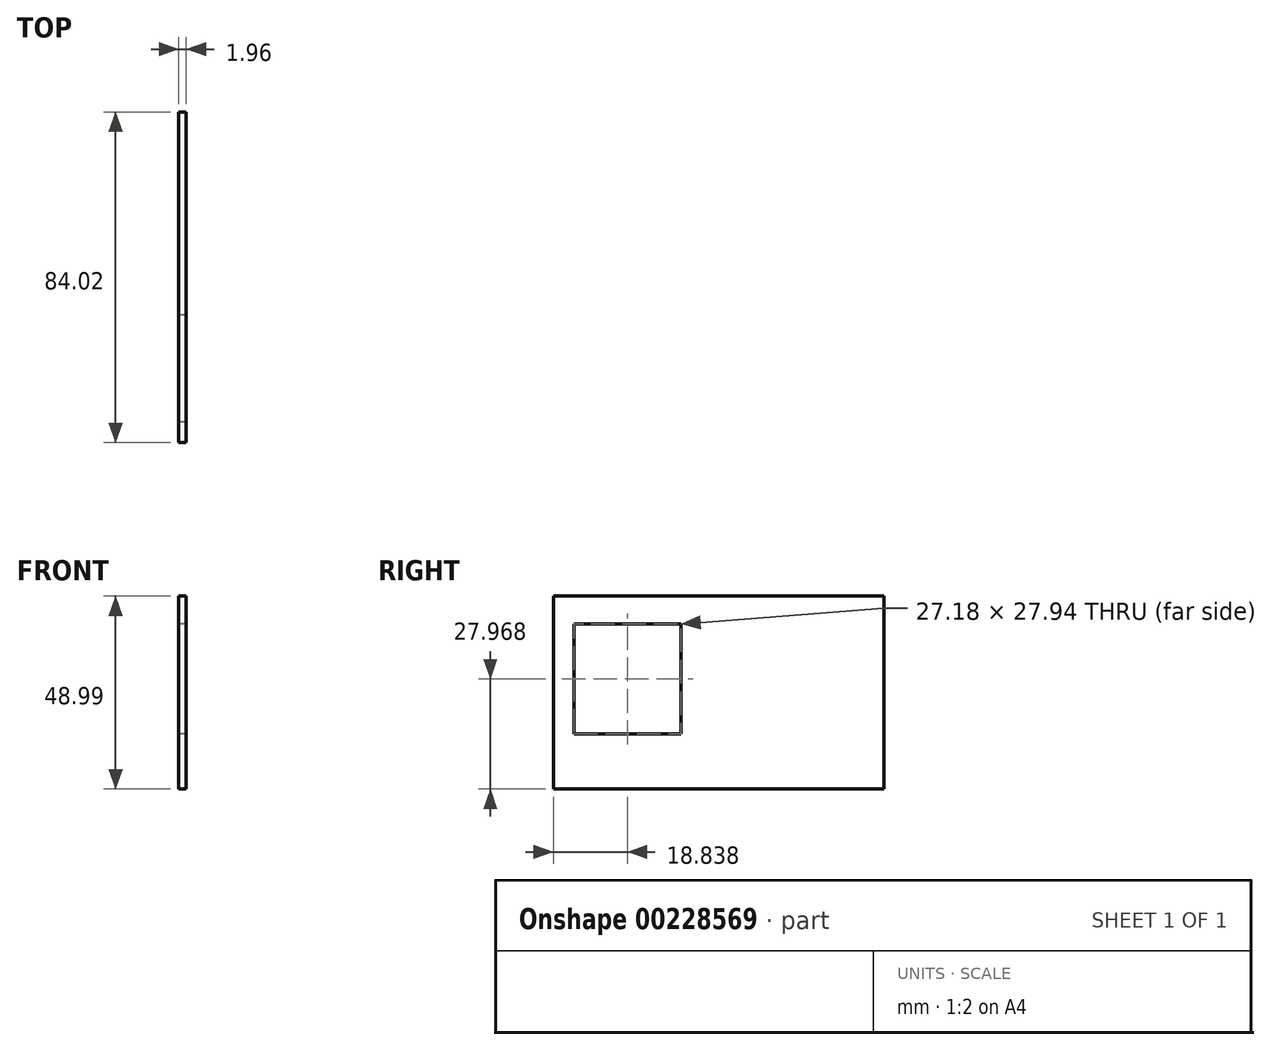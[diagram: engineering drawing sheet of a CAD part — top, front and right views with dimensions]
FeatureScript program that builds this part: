
annotation { "Feature Type Name" : "Feature", "Feature Type Description" : "" }
export const myFeature = defineFeature(function(context is Context, id is Id, definition is map)
    precondition{}
    {
        {
            var Q0;
            Q0=qCreatedBy(makeId("Right.planeOp"),FACE);
            var sketch = newSketch(context, id + "F0", { "sketchPlane" : qUnion([Q0])});
            skLineSegment(sketch, "E0.bottom", {"start": v(0, 0) * mm, "end": v(84.02, 0) * mm});
            skLineSegment(sketch, "E0.top", {"start": v(0, 49) * mm, "end": v(84.02, 49) * mm});
            skLineSegment(sketch, "E0.left", {"start": v(0, 0) * mm, "end": v(0, 49) * mm});
            skLineSegment(sketch, "E0.right", {"start": v(84.02, 0) * mm, "end": v(84.02, 49) * mm});
            skLineSegment(sketch, "E1.bottom", {"start": v(5.25, 14) * mm, "end": v(32.43, 14) * mm});
            skLineSegment(sketch, "E1.top", {"start": v(5.25, 41.94) * mm, "end": v(32.43, 41.94) * mm});
            skLineSegment(sketch, "E1.left", {"start": v(5.25, 14) * mm, "end": v(5.25, 41.94) * mm});
            skLineSegment(sketch, "E1.right", {"start": v(32.43, 14) * mm, "end": v(32.43, 41.94) * mm});
            skSolve(sketch);
        }
        {
            var Q0;
            Q0=makeQuery(id+"F0.imprint","IMPRINT",FACE,{"disambiguationData":[TD([[makeQuery(id+"F0.imprint","IMPRINT",EDGE,{"derivedFrom":sQuery(id+"F0.wireOp",EDGE,"E0.bottom")}),1.0]])]});
            extrude(context, id + "F1", {"entities" : qUnion([Q0]), "depth" : 1.96 * mm});
        }
    });
